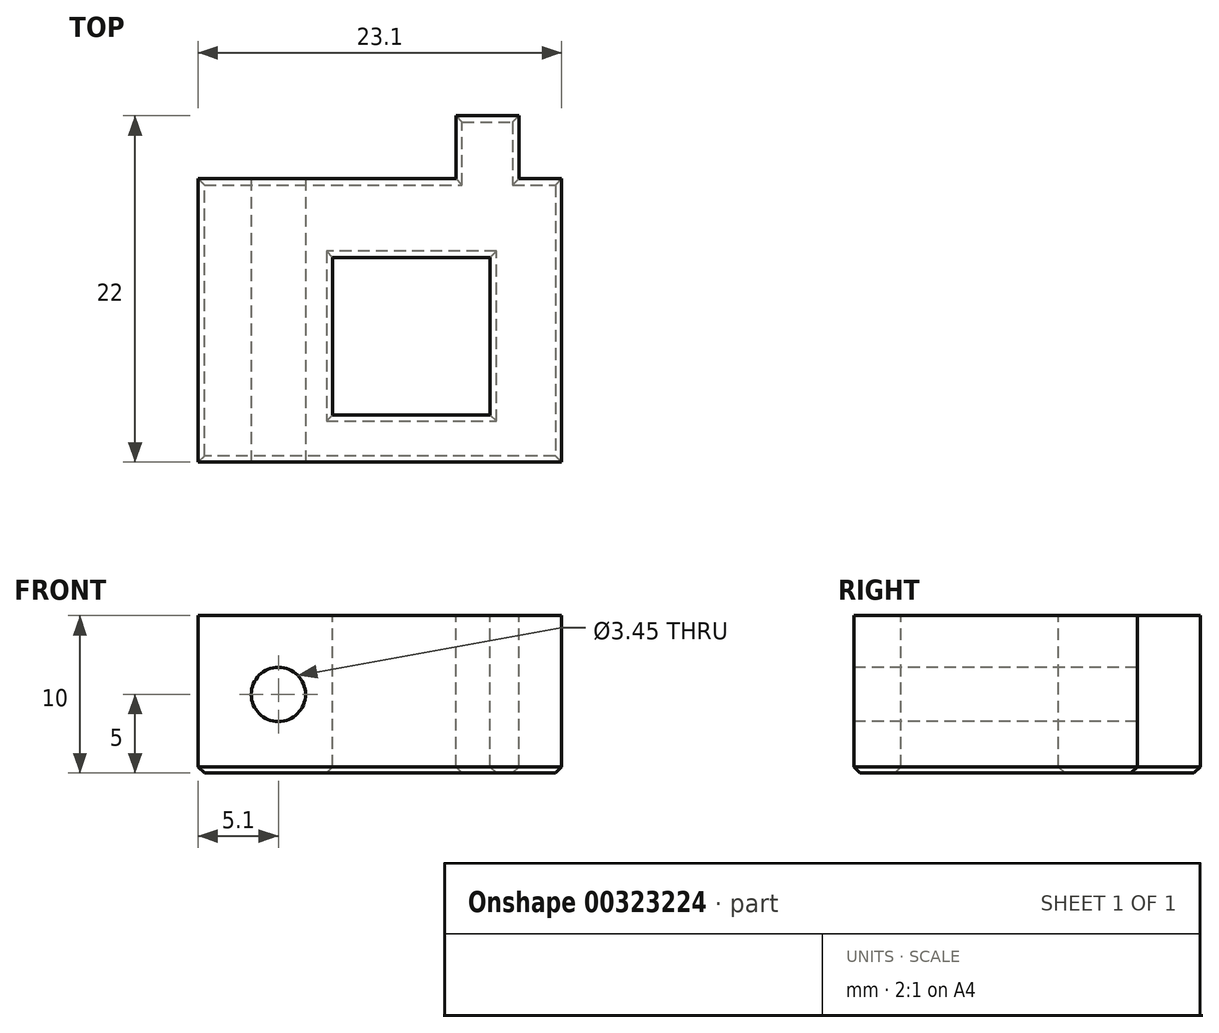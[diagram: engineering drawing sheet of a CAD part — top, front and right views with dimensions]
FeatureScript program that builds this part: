
annotation { "Feature Type Name" : "Feature", "Feature Type Description" : "" }
export const myFeature = defineFeature(function(context is Context, id is Id, definition is map)
    precondition{}
    {
        {
            var Q0;
            Q0=qCreatedBy(makeId("Top.planeOp"),FACE);
            var sketch = newSketch(context, id + "F0", { "sketchPlane" : qUnion([Q0])});
            skLineSegment(sketch, "E0.bottom", {"start": v(0, 0) * mm, "end": v(23.1, 0) * mm});
            skLineSegment(sketch, "E0.top", {"start": v(0, 18) * mm, "end": v(23.1, 18) * mm});
            skLineSegment(sketch, "E0.left", {"start": v(0, 0) * mm, "end": v(0, 18) * mm});
            skLineSegment(sketch, "E0.right", {"start": v(23.1, 0) * mm, "end": v(23.1, 18) * mm});
            skSolve(sketch);
        }
        {
            var Q0;
            Q0=qSketchRegion(id+"F0",true);
            extrude(context, id + "F1", {"entities" : qUnion([Q0]), "depth" : 10 * mm});
        }
        {
            var Q0;
            Q0=makeQuery(id+"F1.opExtrude","CAP_FACE",FACE,{"disambiguationData":[OSD([sQuery(id+"F0.wireOp",EDGE,"E0.bottom"),sQuery(id+"F0.wireOp",EDGE,"E0.top"),sQuery(id+"F0.wireOp",EDGE,"E0.left"),sQuery(id+"F0.wireOp",EDGE,"E0.right")])],"isStart":false});
            var sketch = newSketch(context, id + "F2", { "sketchPlane" : qUnion([Q0])});
            skLineSegment(sketch, "E1.bottom", {"start": v(8.55, 13) * mm, "end": v(18.55, 13) * mm});
            skLineSegment(sketch, "E1.top", {"start": v(8.55, 3) * mm, "end": v(18.55, 3) * mm});
            skLineSegment(sketch, "E1.left", {"start": v(8.55, 13) * mm, "end": v(8.55, 3) * mm});
            skLineSegment(sketch, "E1.right", {"start": v(18.55, 13) * mm, "end": v(18.55, 3) * mm});
            skSolve(sketch);
        }
        {
            var Q0;
            Q0=qSketchRegion(id+"F2",true);
            extrude(context, id + "F3", {"entities" : qUnion([Q0]), "operationType" : NewBodyOperationType.REMOVE, "endBound" : BoundingType.UP_TO_NEXT, "oppositeDirection" : true, "depth" : 25 * mm});
        }
        {
            var Q0;
            Q0=makeQuery(id+"F1.opExtrude","CAP_FACE",FACE,{"disambiguationData":[OSD([sQuery(id+"F0.wireOp",EDGE,"E0.bottom"),sQuery(id+"F0.wireOp",EDGE,"E0.top"),sQuery(id+"F0.wireOp",EDGE,"E0.left"),sQuery(id+"F0.wireOp",EDGE,"E0.right")])],"isStart":false});
            var sketch = newSketch(context, id + "F4", { "sketchPlane" : qUnion([Q0])});
            skLineSegment(sketch, "E2.bottom", {"start": v(16.38, 18) * mm, "end": v(20.38, 18) * mm});
            skLineSegment(sketch, "E2.top", {"start": v(16.38, 22) * mm, "end": v(20.38, 22) * mm});
            skLineSegment(sketch, "E2.left", {"start": v(16.38, 18) * mm, "end": v(16.38, 22) * mm});
            skLineSegment(sketch, "E2.right", {"start": v(20.38, 18) * mm, "end": v(20.38, 22) * mm});
            skSolve(sketch);
        }
        {
            var Q0;
            Q0=makeQuery(id+"F4.imprint","IMPRINT",FACE,{"disambiguationData":[TD([[makeQuery(id+"F4.imprint","IMPRINT",EDGE,{"derivedFrom":sQuery(id+"F4.wireOp",EDGE,"E2.bottom")}),1.0]])]});
            var Q1;
            Q1=makeQuery(id+"F1.opExtrude","CAP_FACE",FACE,{"disambiguationData":[OSD([sQuery(id+"F0.wireOp",EDGE,"E0.bottom"),sQuery(id+"F0.wireOp",EDGE,"E0.top"),sQuery(id+"F0.wireOp",EDGE,"E0.left"),sQuery(id+"F0.wireOp",EDGE,"E0.right")])],"isStart":true});
            extrude(context, id + "F5", {"entities" : qUnion([Q0]), "operationType" : NewBodyOperationType.ADD, "endBound" : BoundingType.UP_TO_SURFACE, "oppositeDirection" : true, "endBoundEntityFace" : qUnion([Q1]), "depth" : 25 * mm});
        }
        {
            var Q0;
            Q0=makeQuery(id+"F1.opExtrude","SWEPT_FACE",FACE,{"disambiguationData":[OSD([sQuery(id+"F0.wireOp",EDGE,"E0.bottom")])]});
            var sketch = newSketch(context, id + "F6", { "sketchPlane" : qUnion([Q0])});
            skCircle(sketch, "E3", {"center": v(5.1, 5) * mm, "radius": 1.73 * mm});
            skSolve(sketch);
        }
        {
            var Q0;
            Q0=qSketchRegion(id+"F6",true);
            extrude(context, id + "F7", {"entities" : qUnion([Q0]), "operationType" : NewBodyOperationType.REMOVE, "endBound" : BoundingType.UP_TO_NEXT, "oppositeDirection" : true, "depth" : 25 * mm});
        }
        {
            var Q0;
            Q0=makeQuery(id+"F5.boolean.opBoolean","MERGE",FACE,{"derivedFrom":[makeQuery(id+"F1.opExtrude","CAP_FACE",FACE,{"disambiguationData":[OSD([sQuery(id+"F0.wireOp",EDGE,"E0.bottom"),sQuery(id+"F0.wireOp",EDGE,"E0.top"),sQuery(id+"F0.wireOp",EDGE,"E0.left"),sQuery(id+"F0.wireOp",EDGE,"E0.right")])],"isStart":true}),makeQuery(id+"F5.opExtrude","CAP_FACE",FACE,{"disambiguationData":[OSD([sQuery(id+"F4.wireOp",EDGE,"E2.bottom"),sQuery(id+"F4.wireOp",EDGE,"E2.top"),sQuery(id+"F4.wireOp",EDGE,"E2.left"),sQuery(id+"F4.wireOp",EDGE,"E2.right")])],"isStart":false})]});
            chamfer(context, id + "F8", {"entities" : qUnion([Q0]), "width" : 0.4 * mm, "tangentPropagation" : true});
        }
    });
